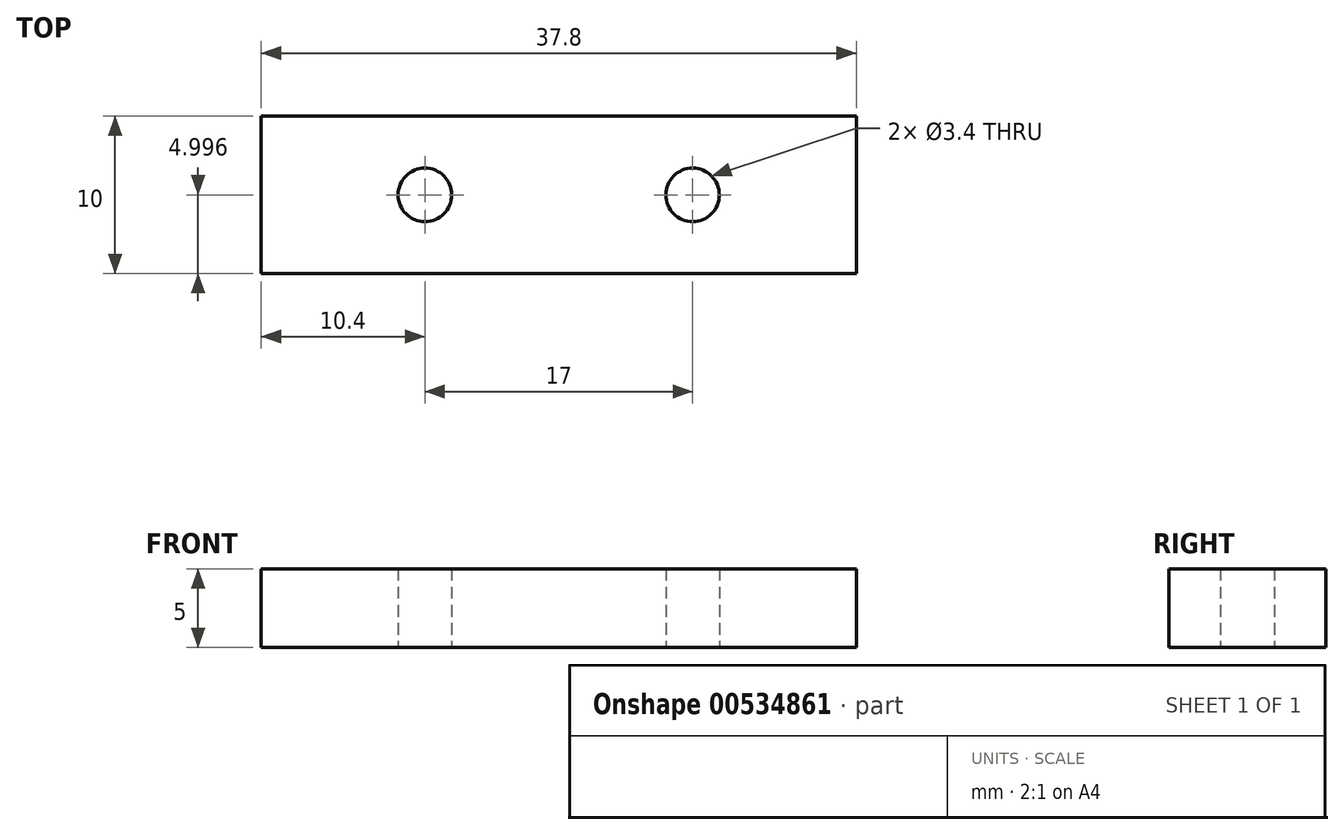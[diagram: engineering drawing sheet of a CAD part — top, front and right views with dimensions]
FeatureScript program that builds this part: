
annotation { "Feature Type Name" : "Feature", "Feature Type Description" : "" }
export const myFeature = defineFeature(function(context is Context, id is Id, definition is map)
    precondition{}
    {
        {
            var Q0;
            Q0=qCreatedBy(makeId("Top.planeOp"),FACE);
            var sketch = newSketch(context, id + "F0", { "sketchPlane" : qUnion([Q0])});
            skLineSegment(sketch, "E0.bottom", {"start": v(-21.75, 22.47) * mm, "end": v(16.05, 22.47) * mm});
            skLineSegment(sketch, "E0.top", {"start": v(-21.75, 12.47) * mm, "end": v(16.05, 12.47) * mm});
            skLineSegment(sketch, "E0.left", {"start": v(-21.75, 22.47) * mm, "end": v(-21.75, 12.47) * mm});
            skLineSegment(sketch, "E0.right", {"start": v(16.05, 22.47) * mm, "end": v(16.05, 12.47) * mm});
            skLineSegment(sketch, "E1", {"start": v(-2.85, 22.47) * mm, "end": v(-2.85, 12.47) * mm});
            skPoint(sketch, "E2", {"position": v(-2.85, 17.47) * mm});
            skCircle(sketch, "E3", {"center": v(-11.35, 17.47) * mm, "radius": 1.7 * mm});
            skCircle(sketch, "E4", {"center": v(5.65, 17.47) * mm, "radius": 1.7 * mm});
            skLineSegment(sketch, "E5", {"start": v(-11.35, 17.47) * mm, "end": v(5.65, 17.47) * mm});
            skSolve(sketch);
        }
        {
            var Q0;
            Q0=qSketchRegion(id+"F0",true);
            var Q1;
            {var subQ4=sQuery(id+"F0.wireOp",EDGE,"E0.left");Q1=makeQuery(id+"F0.imprint","IMPRINT",FACE,{"disambiguationData":[TD([[makeQuery(id+"F0.imprint","IMPRINT",EDGE,{"derivedFrom":subQ4}),1.0]])]});}
            extrude(context, id + "F1", {"entities" : qUnion([Q0, Q1]), "depth" : 5 * mm});
        }
    });
